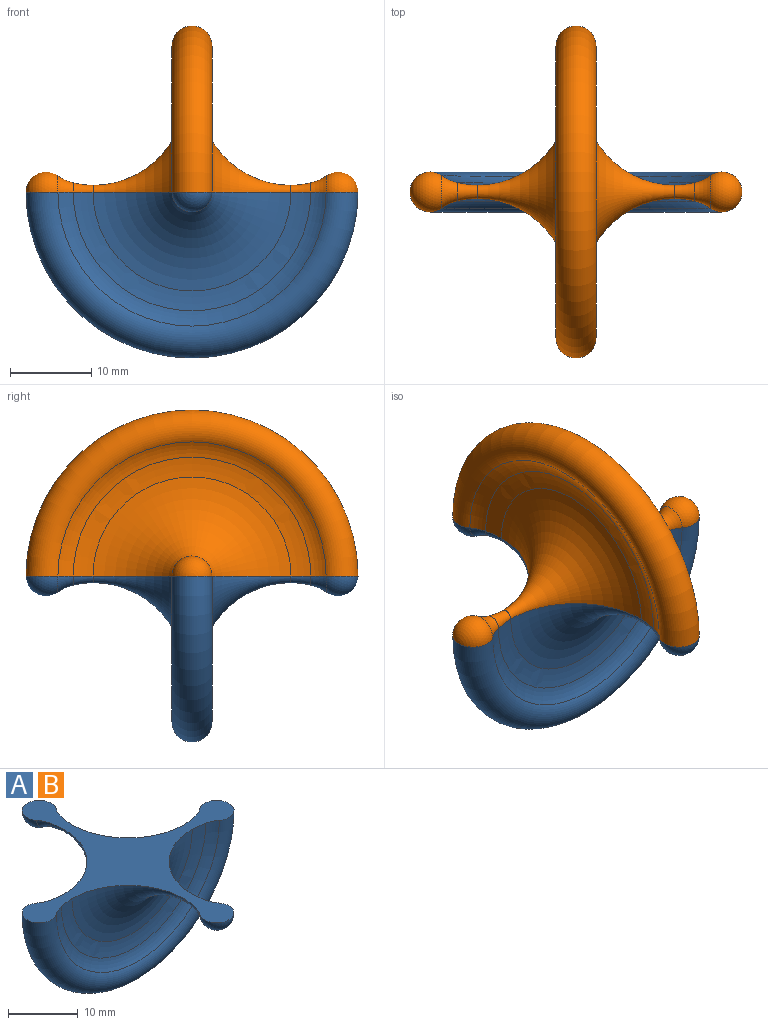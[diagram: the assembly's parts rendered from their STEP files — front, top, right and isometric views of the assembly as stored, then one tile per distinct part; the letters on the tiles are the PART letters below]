
ASSEMBLY  parts=2 mates=1
PART A: 14 faces, bbox 44.2x42.2x22.1 mm
  f0: torus R=13.95mm, axis (0,1,0), area 7.2mm2, adj f1,f12,f13
  f1: torus R=12.17mm, axis (0,1,0), area 277.1mm2, adj f0,f2,f13
  f2: torus R=11.77mm, axis (0,1,0), area 103.5mm2, adj f1,f3,f13
  f3: torus R=13.53mm, axis (0,1,0), area 102.3mm2, adj f2,f4,f13
  f4: torus R=17.96mm, axis (0,1,0), area 644.1mm2, adj f3,f5,f13
  f5: torus R=13.53mm, axis (0,1,0), area 102.3mm2, adj f4,f6,f13
  f6: torus R=11.77mm, axis (0,1,0), area 103.5mm2, adj f5,f7,f13
  f7: torus R=12.17mm, axis (0,1,0), area 277.1mm2, adj f6,f8,f13
  f8: torus R=13.95mm, axis (0,1,0), area 7.2mm2, adj f7,f9,f13
  f9: torus R=6mm, axis (0,1,0), area 9.8mm2, adj f8,f10,f13
  f10: sphere r=2.46mm, area 30.4mm2, adj f9,f13
  f11: sphere r=2.46mm, area 30.4mm2, adj f12,f13
  f12: torus R=6mm, axis (0,1,0), area 9.8mm2, adj f0,f11,f13
  f13: plane 40.85x40.85mm, normal (0,0,1), area 293.2mm2, adj f0,f1,f2,f3,f4,f5,f6,f7
PART B: same geometry as A
PLACE A t=(0.04,-17.99,10.14)mm
PLACE B rot(axis=(-0.71,0.71,0),180deg) t=(18,-0.03,10.14)mm
MATE fastened B.f13 <-> A.f13  axis (0,0,-1) through (0.04,17.93,10.14)mm
